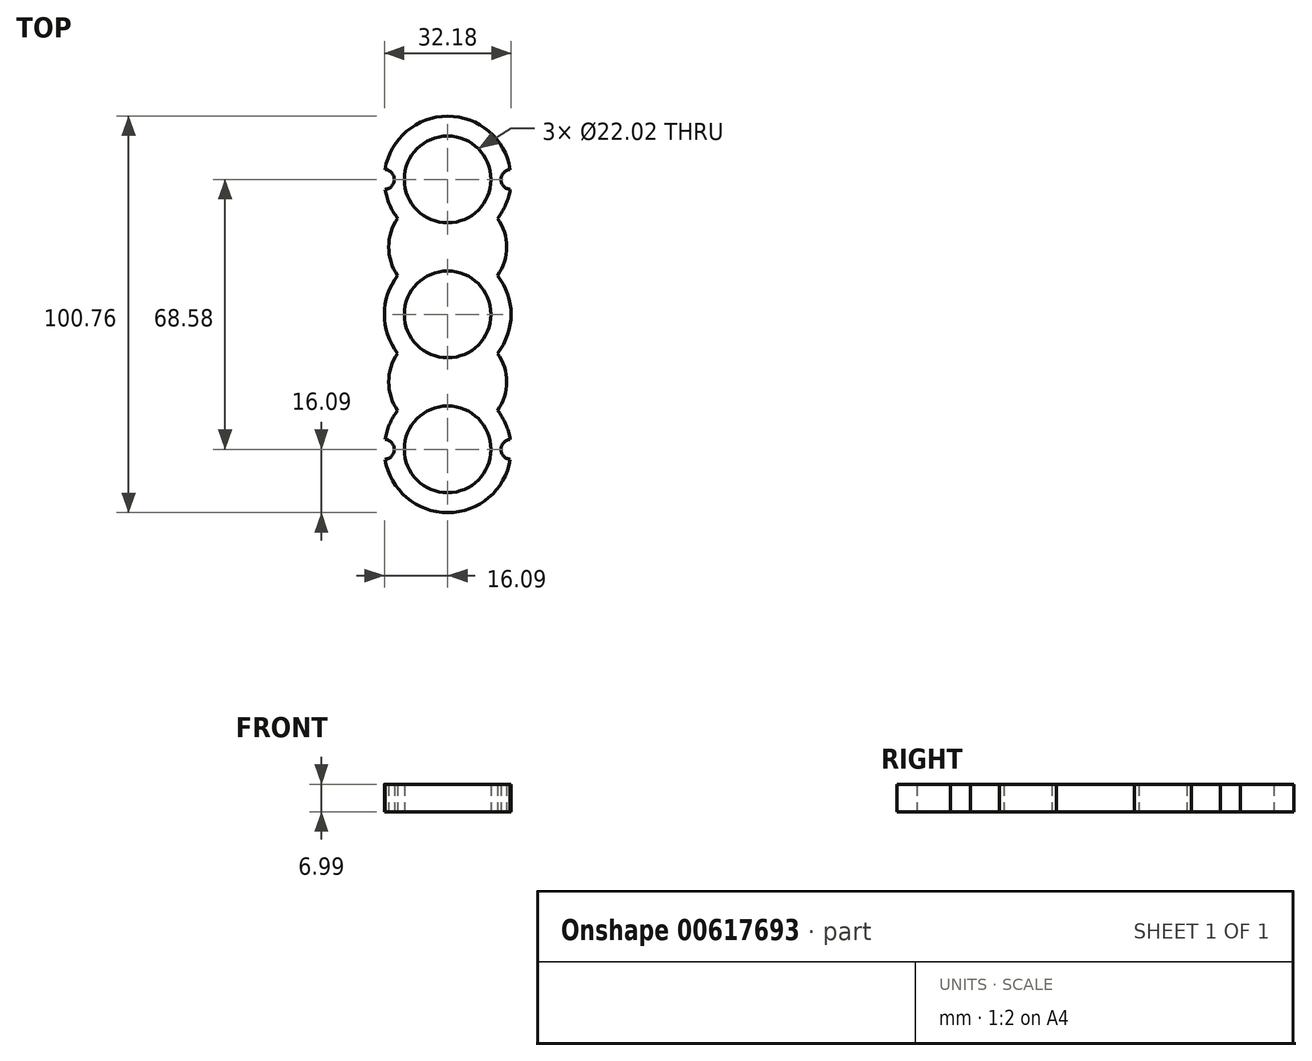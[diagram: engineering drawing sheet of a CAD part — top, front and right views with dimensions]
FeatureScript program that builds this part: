
annotation { "Feature Type Name" : "Feature", "Feature Type Description" : "" }
export const myFeature = defineFeature(function(context is Context, id is Id, definition is map)
    precondition{}
    {
        {
            var Q0;
            Q0=qCreatedBy(makeId("Top.planeOp"),FACE);
            var sketch = newSketch(context, id + "F0", { "sketchPlane" : qUnion([Q0])});
            skCircle(sketch, "E0", {"center": v(0, 0) * mm, "radius": 11.01 * mm});
            skCircle(sketch, "E1", {"center": v(0, 34.3) * mm, "radius": 11.01 * mm});
            skCircle(sketch, "E2", {"center": v(0, -34.3) * mm, "radius": 11.01 * mm});
            skCircle(sketch, "E3", {"center": v(0, 0) * mm, "radius": 16.1 * mm});
            skCircle(sketch, "E4", {"center": v(0, 34.3) * mm, "radius": 16.1 * mm});
            skCircle(sketch, "E5", {"center": v(0, -34.3) * mm, "radius": 16.1 * mm});
            skLineSegment(sketch, "E6", {"start": v(0, 16.1) * mm, "end": v(0, 26.97) * mm});
            skLineSegment(sketch, "E7", {"start": v(0, -16.1) * mm, "end": v(0, -23.28) * mm});
            skArc(sketch, "E8", {"start": v(-12.7, 24.4) * mm, "mid": v(-14.98, 17.15) * mm, "end": v(-12.7, 9.88) * mm});
            skArc(sketch, "E9", {"start": v(12.7, 9.88) * mm, "mid": v(14.98, 17.14) * mm, "end": v(12.7, 24.4) * mm});
            skArc(sketch, "E10", {"start": v(-12.7, -9.88) * mm, "mid": v(-14.98, -17.15) * mm, "end": v(-12.7, -24.4) * mm});
            skArc(sketch, "E11", {"start": v(12.7, -24.4) * mm, "mid": v(14.98, -17.15) * mm, "end": v(12.7, -9.88) * mm});
            skCircle(sketch, "E12", {"center": v(-16.1, 34.3) * mm, "radius": 2.54 * mm});
            skCircle(sketch, "E13", {"center": v(16.1, 34.3) * mm, "radius": 2.54 * mm});
            skCircle(sketch, "E14", {"center": v(-16.1, -34.3) * mm, "radius": 2.54 * mm});
            skLineSegment(sketch, "E15", {"start": v(0, 0) * mm, "end": v(0, 34.3) * mm});
            skLineSegment(sketch, "E16", {"start": v(0, -34.3) * mm, "end": v(0, 0) * mm});
            skLineSegment(sketch, "E17", {"start": v(-16.1, 34.3) * mm, "end": v(16.1, 34.3) * mm});
            skLineSegment(sketch, "E18", {"start": v(-16.1, -34.3) * mm, "end": v(16.1, -34.3) * mm});
            skCircle(sketch, "E19", {"center": v(16.1, -34.3) * mm, "radius": 2.54 * mm});
            skSolve(sketch);
        }
        {
            var Q0;
            {var subQ0=sQuery(id+"F0.wireOp",EDGE,"E9");Q0=makeQuery(id+"F0.imprint","IMPRINT",FACE,{"disambiguationData":[TD([[makeQuery(id+"F0.imprint","IMPRINT",EDGE,{"derivedFrom":subQ0}),1.0]])]});}
            var Q1;
            {var subQ0=sQuery(id+"F0.wireOp",EDGE,"E8");Q1=makeQuery(id+"F0.imprint","IMPRINT",FACE,{"disambiguationData":[TD([[makeQuery(id+"F0.imprint","IMPRINT",EDGE,{"derivedFrom":subQ0}),1.0]])]});}
            var Q2;
            {var subQ0=sQuery(id+"F0.wireOp",EDGE,"E10");Q2=makeQuery(id+"F0.imprint","IMPRINT",FACE,{"disambiguationData":[TD([[makeQuery(id+"F0.imprint","IMPRINT",EDGE,{"derivedFrom":subQ0}),1.0]])]});}
            var Q3;
            {var subQ0=sQuery(id+"F0.wireOp",EDGE,"E11");Q3=makeQuery(id+"F0.imprint","IMPRINT",FACE,{"disambiguationData":[TD([[makeQuery(id+"F0.imprint","IMPRINT",EDGE,{"derivedFrom":subQ0}),1.0]])]});}
            var Q4;
            {var subQ4=sQuery(id+"F0.wireOp",EDGE,"E15");var subQ5=sQuery(id+"F0.wireOp",EDGE,"E0");var subQ6=makeQuery(id+"F0.imprint","INTERSECT",VERTEX,{"derivedFrom":[subQ5,subQ4]});Q4=makeQuery(id+"F0.imprint","IMPRINT",FACE,{"disambiguationData":[TD([[makeQuery(id+"F0.imprint","IMPRINT",EDGE,{"disambiguationData":[TD([[subQ6,-1.0]])],"derivedFrom":subQ5}),-1.0]])]});}
            var Q5;
            {var subQ4=sQuery(id+"F0.wireOp",EDGE,"E15");var subQ5=sQuery(id+"F0.wireOp",EDGE,"E0");var subQ6=makeQuery(id+"F0.imprint","INTERSECT",VERTEX,{"derivedFrom":[subQ5,subQ4]});Q5=makeQuery(id+"F0.imprint","IMPRINT",FACE,{"disambiguationData":[TD([[makeQuery(id+"F0.imprint","IMPRINT",EDGE,{"disambiguationData":[TD([[subQ6,1.0]])],"derivedFrom":subQ5}),-1.0]])]});}
            var Q6;
            {var subQ3=sQuery(id+"F0.wireOp",EDGE,"E17");var subQ8=sQuery(id+"F0.wireOp",EDGE,"E1");var subQ9=makeQuery(id+"F0.imprint","INTERSECT",VERTEX,{"disambiguationData":[OD(0.0)],"derivedFrom":[subQ8,subQ3]});Q6=makeQuery(id+"F0.imprint","IMPRINT",FACE,{"disambiguationData":[TD([[makeQuery(id+"F0.imprint","IMPRINT",EDGE,{"disambiguationData":[TD([[subQ9,1.0]])],"derivedFrom":subQ8}),-1.0]])]});}
            var Q7;
            {var subQ6=sQuery(id+"F0.wireOp",EDGE,"E17");var subQ8=sQuery(id+"F0.wireOp",EDGE,"E1");var subQ9=makeQuery(id+"F0.imprint","INTERSECT",VERTEX,{"disambiguationData":[OD(0.0)],"derivedFrom":[subQ8,subQ6]});Q7=makeQuery(id+"F0.imprint","IMPRINT",FACE,{"disambiguationData":[TD([[makeQuery(id+"F0.imprint","IMPRINT",EDGE,{"disambiguationData":[TD([[subQ9,-1.0]])],"derivedFrom":subQ8}),-1.0]])]});}
            var Q8;
            {var subQ4=sQuery(id+"F0.wireOp",EDGE,"E17");var subQ8=sQuery(id+"F0.wireOp",EDGE,"E1");var subQ9=makeQuery(id+"F0.imprint","INTERSECT",VERTEX,{"disambiguationData":[OD(1.0)],"derivedFrom":[subQ8,subQ4]});Q8=makeQuery(id+"F0.imprint","IMPRINT",FACE,{"disambiguationData":[TD([[makeQuery(id+"F0.imprint","IMPRINT",EDGE,{"disambiguationData":[TD([[subQ9,1.0]])],"derivedFrom":subQ8}),-1.0]])]});}
            var Q9;
            {var subQ0=sQuery(id+"F0.wireOp",EDGE,"E16");var subQ1=sQuery(id+"F0.wireOp",EDGE,"E2");var subQ2=makeQuery(id+"F0.imprint","INTERSECT",VERTEX,{"derivedFrom":[subQ1,subQ0]});Q9=makeQuery(id+"F0.imprint","IMPRINT",FACE,{"disambiguationData":[TD([[makeQuery(id+"F0.imprint","IMPRINT",EDGE,{"disambiguationData":[TD([[subQ2,1.0]])],"derivedFrom":subQ1}),-1.0]])]});}
            var Q10;
            {var subQ6=sQuery(id+"F0.wireOp",EDGE,"E16");var subQ8=sQuery(id+"F0.wireOp",EDGE,"E2");var subQ9=makeQuery(id+"F0.imprint","INTERSECT",VERTEX,{"derivedFrom":[subQ8,subQ6]});Q10=makeQuery(id+"F0.imprint","IMPRINT",FACE,{"disambiguationData":[TD([[makeQuery(id+"F0.imprint","IMPRINT",EDGE,{"disambiguationData":[TD([[subQ9,-1.0]])],"derivedFrom":subQ8}),-1.0]])]});}
            var Q11;
            {var subQ0=sQuery(id+"F0.wireOp",EDGE,"E18");var subQ1=sQuery(id+"F0.wireOp",EDGE,"E2");var subQ9=makeQuery(id+"F0.imprint","INTERSECT",VERTEX,{"disambiguationData":[OD(0.0)],"derivedFrom":[subQ1,subQ0]});Q11=makeQuery(id+"F0.imprint","IMPRINT",FACE,{"disambiguationData":[TD([[makeQuery(id+"F0.imprint","IMPRINT",EDGE,{"disambiguationData":[TD([[subQ9,1.0]])],"derivedFrom":subQ1}),-1.0]])]});}
            extrude(context, id + "F1", {"entities" : qUnion([Q0, Q1, Q2, Q3, Q4, Q5, Q6, Q7, Q8, Q9, Q10, Q11]), "depth" : 7 * mm, "offsetDistance" : 25.4 * mm});
        }
    });
